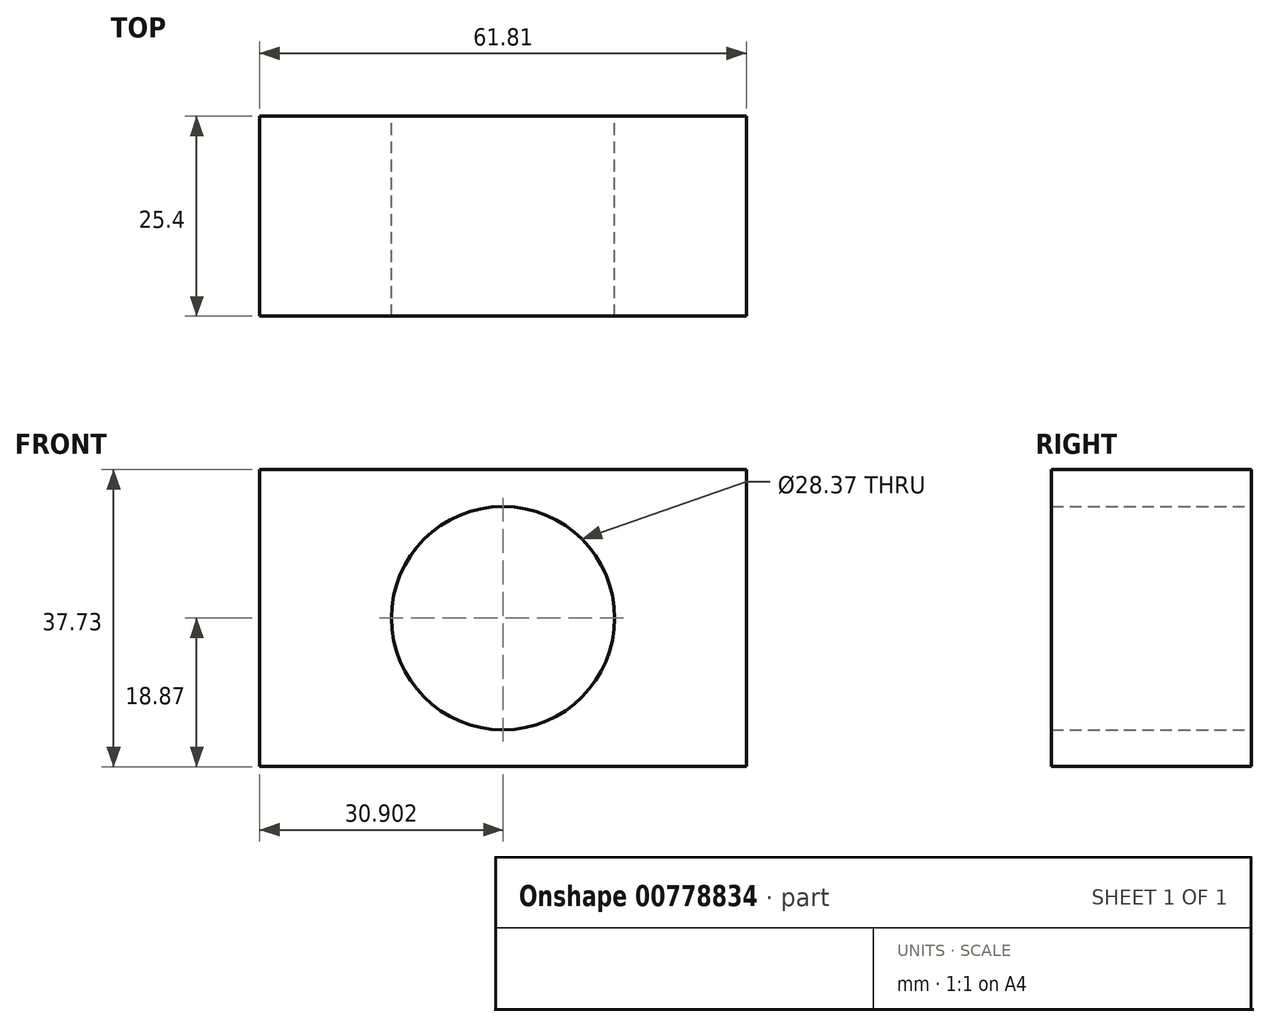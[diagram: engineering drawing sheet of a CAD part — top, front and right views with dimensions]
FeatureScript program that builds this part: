
annotation { "Feature Type Name" : "Feature", "Feature Type Description" : "" }
export const myFeature = defineFeature(function(context is Context, id is Id, definition is map)
    precondition{}
    {
        {
            var Q0;
            Q0=qCreatedBy(makeId("Front.planeOp"),FACE);
            var sketch = newSketch(context, id + "F0", { "sketchPlane" : qUnion([Q0])});
            skLineSegment(sketch, "E0.bottom", {"start": v(-90.91, 56.6) * mm, "end": v(-29.1, 56.6) * mm});
            skLineSegment(sketch, "E0.top", {"start": v(-90.91, 18.86) * mm, "end": v(-29.1, 18.86) * mm});
            skLineSegment(sketch, "E0.left", {"start": v(-90.91, 56.6) * mm, "end": v(-90.91, 18.86) * mm});
            skLineSegment(sketch, "E0.right", {"start": v(-29.1, 56.6) * mm, "end": v(-29.1, 18.86) * mm});
            skCircle(sketch, "E1", {"center": v(-60, 37.73) * mm, "radius": 14.18 * mm});
            skPoint(sketch, "E2", {"position": v(-29.1, 37.73) * mm});
            skPoint(sketch, "E3", {"position": v(-60, 56.6) * mm});
            skSolve(sketch);
        }
        {
            var Q0;
            Q0 = qSketchRegion(id + "F0", true);
            extrude(context, id + "F1", {"entities" : qUnion([Q0]), "depth" : 25.4 * mm, "offsetDistance" : 25.4 * mm});
        }
    });
